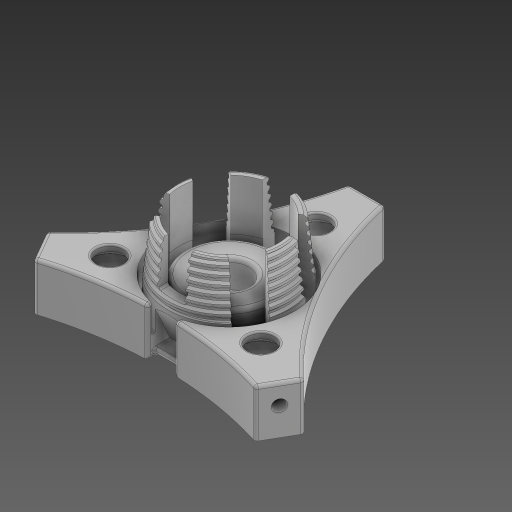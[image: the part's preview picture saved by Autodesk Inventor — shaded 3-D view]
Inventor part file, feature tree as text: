
AUTODESK INVENTOR PART (.ipt)
format: ipt  version: 2024 (Build 280153000, 153)  size: 1,712,640 bytes
history: native  units: mm
features: sketch x17, extrude x12, fillet x9, chamfer x3, hole x3, draft x2, helix x2, plane x2, pattern_circular x2, projected_geometry x2
ambient origin geometry x8: Origin, YZ Plane, XZ Plane, XY Plane, X Axis, Y Axis, Z Axis, Center Point
bodies: Solid1 (feature_tree)
feature tree (54):
  extrude  "Extrusion1"  Depth=29.5mm
  draft  "FaceDraft1"
  sketch  "Sketch2"  dims[d7=6.806784mm d8=0.55605mm]
  helix  "Coil1"  [1 undecoded]
  helix  "Coil2"  [1 undecoded]
  extrude  "Extrusion2"  Depth=0.55605mm
  extrude  "Extrusion3"  TaperAngle=0.0deg  [1 undecoded]
  fillet  "Fillet1"  [1 undecoded]
  chamfer  "Chamfer1"  Distance=0.3mm Angle=45.0deg
  plane  "Work Plane1"
  extrude  "Extrusion4"  TaperAngle=0.0deg  [1 undecoded]
  extrude  "Extrusion8"  Depth=60.0mm TaperAngle=360.0deg
  hole  "Hole2"  [1 undecoded]
  sketch  "Sketch13"  dims[d58=6.0mm d65=60.0mm d67=360.0deg]
  extrude  "Extrusion11"  Depth=10.0mm TaperAngle=0.0deg
  hole  "Bearing Hole"  [1 undecoded]
  pattern_circular  "Circular Pattern4"  Count=3 Angle=360.0deg
  extrude  "Extrusion13"  Depth=7.0mm TaperAngle=0.0deg
  sketch  "Sketch20"  dims[d126=6.804mm d127=6.0mm d128=9.979mm d129=8.89mm d130=90.0deg d131=8.0mm d132=20.594885mm d133=22.0mm d134=30.0mm d135=360.0deg]
  extrude  "Extrusion14"  Depth=1.55mm TaperAngle=45.0deg
  sketch  "Sketch18"  dims[d124=34.0mm]
  fillet  "Fillet9"  Radius=0.24mm
  chamfer  "Chamfer4"  [1 undecoded]
  chamfer  "Chamfer5"  Distance=0.5mm
  fillet  "Fillet11"  Radius=2.0mm
  draft  "FaceDraft2"
  fillet  "Fillet13"  Radius=34.767mm
  extrude  "Extrusion15"  Depth=0.5mm
  hole  "Hole5"  [1 undecoded]
  pattern_circular  "Circular Pattern5"  [2 undecoded]
  plane  "Work Plane4"
  extrude  "Extrusion16"  Depth=0.5mm
  fillet  "Fillet14"  Radius=30.0mm
  fillet  "Fillet16"  Radius=16.0mm
  extrude  "Extrusion17"  TaperAngle=0.0deg  [1 undecoded]
  extrude  "Extrusion19"  Depth=0.5mm
  fillet  "Fillet17"  Radius=0.4mm
  fillet  "Fillet18"  Radius=25.0mm
  fillet  "Fillet19"  Radius=22.0mm
  sketch  "Sketch1"  dims[d0=24.7mm d1=29.5mm d2=12.875mm d3=0.0mm d4=1.047198mm]
  projected_geometry  "Projected Loop1"
  sketch  "Sketch3"  dims[d9=6.806784mm]
  sketch  "Sketch4"  dims[d10=2.0mm d11=10.0mm d12=70.0mm d13=-1.047198mm d14=90.0deg d15=90.0deg d16=0.0mm d17=0.0mm d18=0.6mm]
  sketch  "Sketch5"  dims[d19=2.0mm d20=10.0mm d21=10.0mm d22=1.047198mm d23=90.0deg d24=90.0deg d25=0.0mm d26=0.0mm d27=0.0mm d28=0.0mm d29=0.0mm d30=0.0mm]
  sketch  "Sketch10"  dims[d31=0.6mm d32=0.3mm d33=2.0mm d34=45.0deg]
  sketch  "Sketch11"  dims[d36=-2.0mm d42=0.0mm d43=0.0mm]
  sketch  "Sketch15"  dims[d91=33.0mm d92=12.0mm d93=0.0mm]
  sketch  "Sketch17"  dims[d94=5.3mm d95=6.0mm d96=10.0mm d97=7.0mm d98=90.0deg d99=8.0mm d100=20.594885mm d122=10.0mm d123=0.0mm]
  sketch  "Sketch21"  dims[d146=11.34464mm d147=7.0mm d148=0.0mm]
  sketch  "Sketch22"  dims[d150=1.0mm d151=1.55mm d152=2.0mm d153=45.0deg]
  sketch  "Sketch25"  dims[d154=0.5mm d155=2.0mm d156=45.0deg d158=0.24mm]
  sketch  "Sketch26"  dims[d160=1.25mm d161=0.0mm d162=0.0mm]
  sketch  "Sketch28"  dims[d163=30.0deg d164=0.5mm d165=2.0mm d166=34.767mm d167=9.0mm d168=30.0deg d169=7.0mm d170=0.0mm d171=3.0mm d172=6.0mm d173=9.779mm d174=7.62mm d175=90.0deg d176=7.0mm d177=0.0mm d178=5.0mm d179=30.0mm d180=360.0deg d182=16.0mm d183=0.0mm d184=0.0mm d185=0.75mm d187=0.4mm d188=25.0mm d189=22.0mm d190=31.0mm d191=7.0mm d192=0.0mm d193=32.8mm d208=9.0mm d209=0.0mm d210=1.0mm d211=0.25mm d212=0.5mm d213=7.0mm d214=60.0mm d216=360.0deg]
  projected_geometry  "Project Cut Edges3"
note: 12 required parameter values undecoded (feature->parameter linkage not recoverable at this tier; creation-order binding heuristic only, values carry confidence <= 0.55)
